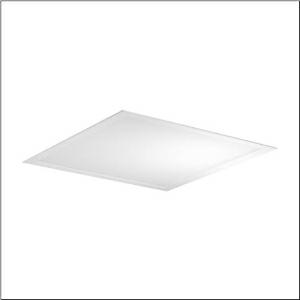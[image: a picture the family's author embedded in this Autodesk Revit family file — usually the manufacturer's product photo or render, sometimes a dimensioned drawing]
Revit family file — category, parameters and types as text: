
# Revit family: apollon_21_square_51mq11wd2614
name_source: partatom
category: Lighting Fixtures
units: mm (PartAtom-declared; Revit-internal decimal feet)

## family parameters
Cut with Voids When Loaded = No
Host = Face
Light Source = No
Part Type = Normal
Room Calculation Point = No
Round Connector Dimension = Use Diameter
Shared = No

## types (1)
- Apollon 21 square (1 x LED, 4150 lm, 24.7 W, 6500K)
    Apparent Load = 25 VA
    CIE Flux Codes = 60 87 97 100 100
    Color Rendering = 80
    Color Temperature = 6500K
    Default Elevation = 1800 mm
    Description = Apollon 21 square, office luminaire, primary optical cover: micro prismatic cover, of PMMA, CAT 2 (L<= 3000cd/m²), light emission: direct distribution, primary light characteristic: symmetric, installation type: lay-in mounting, LED, rated luminous flux: 4.150lm, luminous efficacy: 168lm/W, light colour: 865, colour temperature: 6500K, control gear: DALI 2, Multilumen, with terminal, 5-pole, mains connection: 220..240V, AC/DC, 0/50..60Hz, rated input power: 24.7W, suitable for self-contained emergency lighting element 59MQE002602A with integrated self-test function according to EN 60598-2-22, housing, of aluminium, coated, traffic white (RAL 9016), module: M625, length: 620mm, width: 620mm, height: 55mm, recess depth: 180mm, housing upper side, of sheet steel, galvanised, protection rating (complete): IP20, protection rating (lamp compartment, on room side): IP50, insulation class (complete): insulation class II (safety insulation), certification: CE, ENEC, impact resistance: IK03, permissible operating ambient temperature: -20..+45°C, permissible storage temperature: -40..+80°C, standard: EN 60598-2-22, packaging unit: 1 piece
    Height = 0 mm  [stored 0 ft]
    Lamp = 1 x LED
    Lamp Light Flux = 4150 lm
    Lamp Power = 24.7 W
    Lamp count = 1
    Length = 620 mm
    Luminous efficacy = 168 lm/W
    Manufacturer = Siteco
    ModVariant = No
    Model = 51MQ11WD2614
    Mounting Place = Ceiling
    Mounting Type = Recessed
    Number of Poles = 1
    OnlyDefault = Yes
    Power Factor = 1
    Product Name = Apollon 21 square
    Product group = office luminaire | ceiling recessed
    ProductGroupID = 400
    Protection Class = Protection class II
    Protection Degree = IP 20
    RLX_Detail_Level = 1
    RLX_Emergency_Light_Flux = 0 lm
    RLX_Emergency_Type = 0
    RLX_Emergency_Type_DB = No
    RlxData = <blob elided: 13165 chars, md5=552b421f>
    Socket = socket
    Standby Power = 0 W
    System Light Flux = 4150 lm
    System Power = 25 W
    Type Comments = Product without accessories
    Type Image = l_1291054.jpg
    URL = http://relux.com
    VarID = ---
    Voltage = 0 V
    Weight = 0.00 kg
    Width = 620 mm

note: [stored X ft] marks values corroborated as IEEE doubles in the binary element streams (Revit-internal decimal feet)

## geometry (parser evidence)
native form markers: Sweep x10
no freeform markers — native parametric forms only
